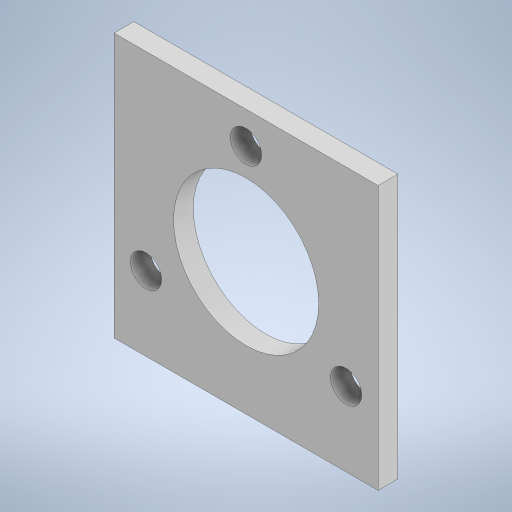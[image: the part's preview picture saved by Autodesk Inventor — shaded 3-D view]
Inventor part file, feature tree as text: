
AUTODESK INVENTOR PART (.ipt)
format: ipt  version: 2024 (Build 280153000, 153)  size: 275,456 bytes
history: native  units: in
note: dims shown in document units (in); Inventor stores cm internally (conversion verified against a paired STEP export)
features: extrude x1, sketch x1
ambient origin geometry x8: Origin, YZ Plane, XZ Plane, XY Plane, X Axis, Y Axis, Z Axis, Center Point
bodies: Solid1 (feature_tree)
feature tree (2):
  extrude  "Extrusion1"  Depth=1.5748in
  sketch  "Sketch1"  dims[d0=1.5748in d1=1.5748in d2=0.8661in d3=0.5967in d4=0.5967in d5=120.0deg d6=0.5967in d7=120.0deg d8=0.1856in d9=0.1856in d10=0.1856in d11=0.1181in d12=0.0in d13=0.0197in d14=0.0344in]
